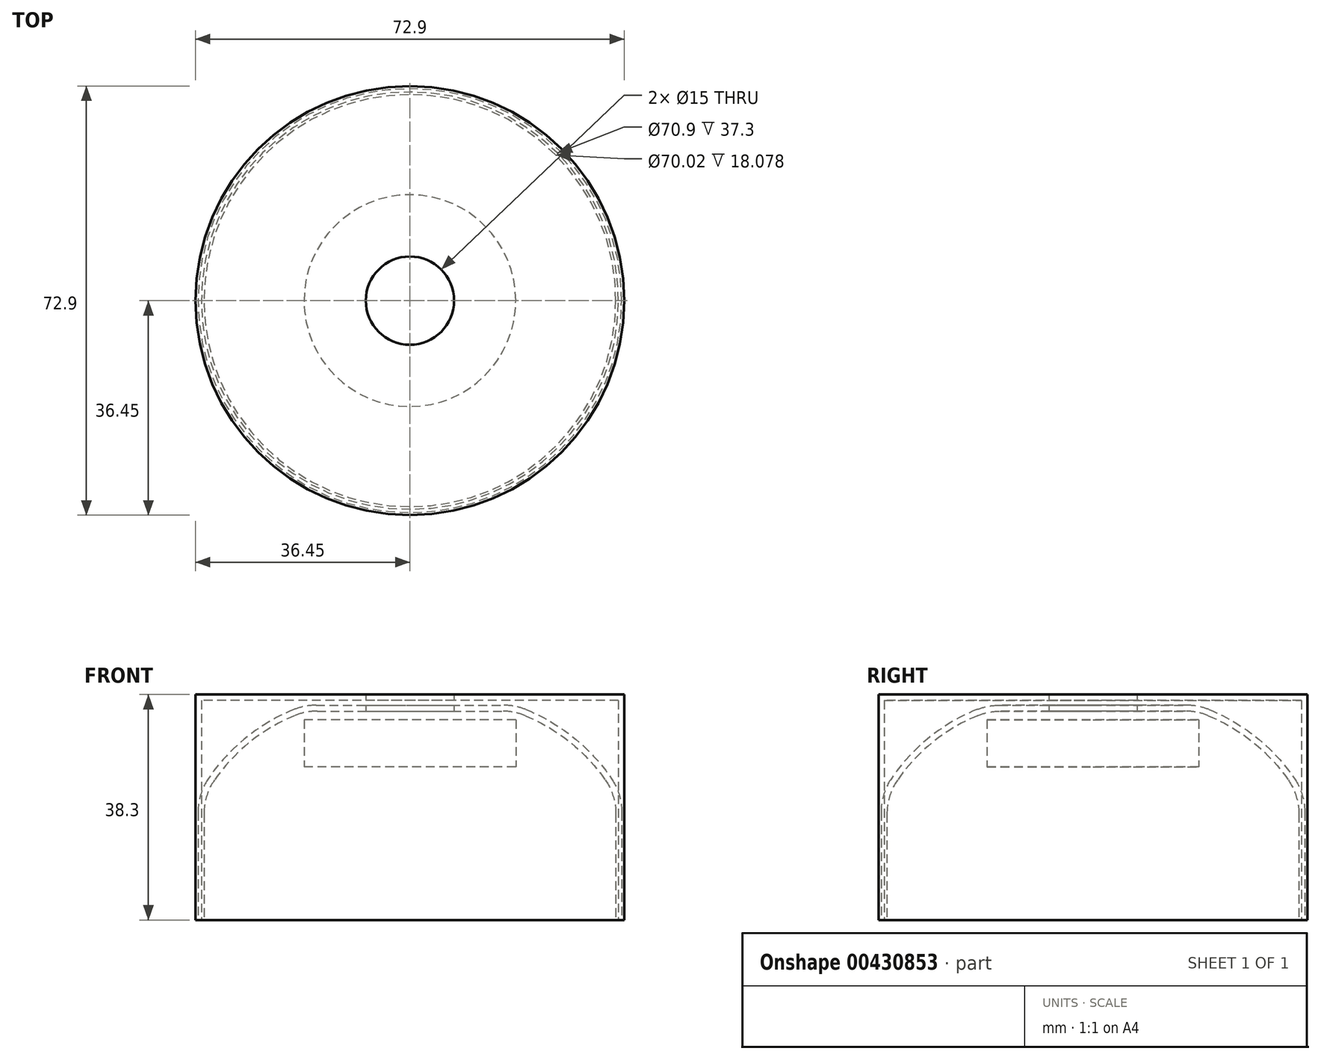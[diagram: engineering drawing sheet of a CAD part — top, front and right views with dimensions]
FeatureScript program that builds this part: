
annotation { "Feature Type Name" : "Feature", "Feature Type Description" : "" }
export const myFeature = defineFeature(function(context is Context, id is Id, definition is map)
    precondition{}
    {
        {
            assignVariable(context, id + "F0", {"name" : "Tollerance", "anyValue" : .9});
        }
        {
            assignVariable(context, id + "F1", {"name" : "FanThickness", "anyValue" : 8});
        }
        {
            assignVariable(context, id + "F2", {"name" : "FanHieght", "anyValue" : 34});
        }
        {
            assignVariable(context, id + "F3", {"name" : "Hieght", "anyValue" : 35.5});
        }
        {
            assignVariable(context, id + "F4", {"name" : "ShellThickness", "anyValue" : 1});
        }
        {
            var Q0;
            Q0=qCreatedBy(makeId("Top.planeOp"),FACE);
            var sketch = newSketch(context, id + "F5", { "sketchPlane" : qUnion([Q0])});
            skCircle(sketch, "E0", {"center": v(0, 0) * mm, "radius": 35.45 * mm});
            skCircle(sketch, "E1.0", {"center": v(0, 0) * mm, "radius": 36.45 * mm});
            skSolve(sketch);
        }
        {
            var Q0;
            Q0=qCreatedBy(makeId("Top.planeOp"),FACE);
            cPlane(context, id + "F6", {"entities" : qUnion([Q0]), "cplaneType" : CPlaneType.OFFSET, "offset" : ((getVariable(context, 'FanHieght')) - getVariable(context, 'FanThickness')) * mm, "width" : 150 * mm, "height" : 150 * mm});
        }
        {
            var Q0;
            Q0=qCreatedBy(id+"F6.planeOp",FACE);
            var sketch = newSketch(context, id + "F7", { "sketchPlane" : qUnion([Q0])});
            skCircle(sketch, "E2", {"center": v(0, 0) * mm, "radius": 18 * mm});
            skSolve(sketch);
        }
        {
            var Q0;
            Q0=makeQuery(id+"F7.imprint","IMPRINT",FACE,{"disambiguationData":[TD([[makeQuery(id+"F7.imprint","IMPRINT",EDGE,{"derivedFrom":sQuery(id+"F7.wireOp",EDGE,"E2")}),1.0]])]});
            extrude(context, id + "F8", {"entities" : qUnion([Q0]), "depth" : (getVariable(context, 'FanThickness')) * mm});
        }
        {
            var Q0;
            Q0=makeQuery(id+"F5.imprint","IMPRINT",FACE,{"disambiguationData":[TD([[makeQuery(id+"F5.imprint","IMPRINT",EDGE,{"derivedFrom":sQuery(id+"F5.wireOp",EDGE,"E0")}),-1.0]])]});
            extrude(context, id + "F9", {"entities" : qUnion([Q0]), "depth" : (getVariable(context, 'Hieght') + (2 * getVariable(context, 'Tollerance'))) * mm});
        }
        {
            var Q0;
            Q0=makeQuery(id+"F9.opExtrude","CAP_FACE",FACE,{"disambiguationData":[OSD([sQuery(id+"F5.wireOp",EDGE,"E0"),sQuery(id+"F5.wireOp",EDGE,"E1.0")])],"isStart":false});
            cPlane(context, id + "F10", {"entities" : qUnion([Q0]), "cplaneType" : CPlaneType.OFFSET, "offset" : 0 * mm, "width" : 150 * mm, "height" : 150 * mm});
        }
        {
            var Q0;
            Q0=qCreatedBy(id+"F10.planeOp",FACE);
            var sketch = newSketch(context, id + "F11", { "sketchPlane" : qUnion([Q0])});
            skCircle(sketch, "E3", {"center": v(0, 0) * mm, "radius": 36.45 * mm});
            skCircle(sketch, "E4", {"center": v(0, 0) * mm, "radius": 7.5 * mm});
            skSolve(sketch);
        }
        {
            var Q0;
            Q0=makeQuery(id+"F11.imprint","IMPRINT",FACE,{"disambiguationData":[TD([[makeQuery(id+"F11.imprint","IMPRINT",EDGE,{"derivedFrom":sQuery(id+"F11.wireOp",EDGE,"E3")}),1.0]])]});
            extrude(context, id + "F12", {"entities" : qUnion([Q0]), "operationType" : NewBodyOperationType.ADD, "depth" : (getVariable(context, 'ShellThickness')) * mm});
        }
        {
            var Q0;
            Q0=qCreatedBy(makeId("Front.planeOp"),FACE);
            var sketch = newSketch(context, id + "F13", { "sketchPlane" : qUnion([Q0])});
            skLineSegment(sketch, "E5", {"start": v(0, 0) * mm, "end": v(0, 37.85) * mm, "construction": true});
            skLineSegment(sketch, "E6", {"start": v(35.01, 0) * mm, "end": v(35.01, 18.08) * mm});
            skArc(sketch, "E7", {"start": v(33.2, 23.82) * mm, "mid": v(27.18, 30.24) * mm, "end": v(19.6, 34.73) * mm});
            skArc(sketch, "E8.1", {"start": v(34.28, 24) * mm, "mid": v(27.87, 30.97) * mm, "end": v(19.71, 35.76) * mm});
            skLineSegment(sketch, "E8.2", {"start": v(36.01, 0) * mm, "end": v(36.01, 18.39) * mm});
            skLineSegment(sketch, "E9", {"start": v(36.01, 0) * mm, "end": v(35.01, 0) * mm});
            skPoint(sketch, "E10.visualSharp", {"position": v(35.01, 20.9) * mm});
            skArc(sketch, "E10.filletArc", {"start": v(35.01, 18.08) * mm, "mid": v(34.55, 21.09) * mm, "end": v(33.2, 23.82) * mm});
            skPoint(sketch, "E11.visualSharp", {"position": v(36.01, 21.16) * mm});
            skArc(sketch, "E11.filletArc", {"start": v(36.01, 18.39) * mm, "mid": v(35.57, 21.33) * mm, "end": v(34.28, 24) * mm});
            skPoint(sketch, "E12.visualSharp", {"position": v(17.57, 35.49) * mm});
            skArc(sketch, "E12.filletArc", {"start": v(19.6, 34.73) * mm, "mid": v(17.73, 35.3) * mm, "end": v(15.78, 35.49) * mm});
            skPoint(sketch, "E13.visualSharp", {"position": v(17.73, 36.49) * mm});
            skArc(sketch, "E13.filletArc", {"start": v(19.71, 35.76) * mm, "mid": v(17.88, 36.3) * mm, "end": v(15.97, 36.49) * mm});
            skLineSegment(sketch, "E14", {"start": v(7.5, 35.49) * mm, "end": v(15.78, 35.49) * mm});
            skLineSegment(sketch, "E15", {"start": v(7.5, 36.49) * mm, "end": v(15.97, 36.49) * mm});
            skLineSegment(sketch, "E16", {"start": v(7.5, 36.49) * mm, "end": v(7.5, 35.49) * mm});
            skSolve(sketch);
        }
        {
            var Q0;
            Q0=makeQuery(id+"F13.imprint","IMPRINT",FACE,{"disambiguationData":[TD([[makeQuery(id+"F13.imprint","IMPRINT",EDGE,{"derivedFrom":sQuery(id+"F13.wireOp",EDGE,"E6")}),-1.0]])]});
            var Q1;
            Q1=sQuery(id+"F13.wireOp",EDGE,"E5");
            revolve(context, id + "F14", {"entities" : qUnion([Q0]), "axis" : qUnion([Q1]), "revolveType" : RevolveType.FULL});
        }
    });
